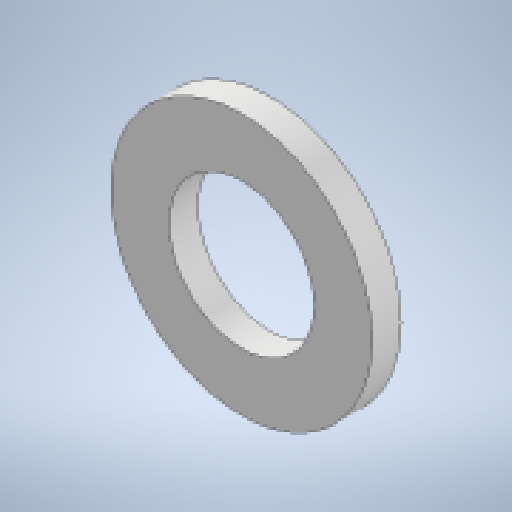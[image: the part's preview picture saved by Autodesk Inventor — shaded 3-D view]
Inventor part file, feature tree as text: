
AUTODESK INVENTOR PART (.ipt)
format: ipt  version: 2023 (Build 270158000, 158)  size: 135,168 bytes
history: native  units: in
note: dims shown in document units (in); Inventor stores cm internally (conversion verified against a paired STEP export)
features: extrude x1, sketch x1
ambient origin geometry x8: Origin, YZ Plane, XZ Plane, XY Plane, X Axis, Y Axis, Z Axis, Center Point
bodies: Solid1 (feature_tree)
feature tree (2):
  extrude  "Extrusion1"  Depth=0.0394in
  sketch  "Sketch1"  dims[d0=0.1969in d1=0.3543in d2=0.0394in d3=0.0in]
